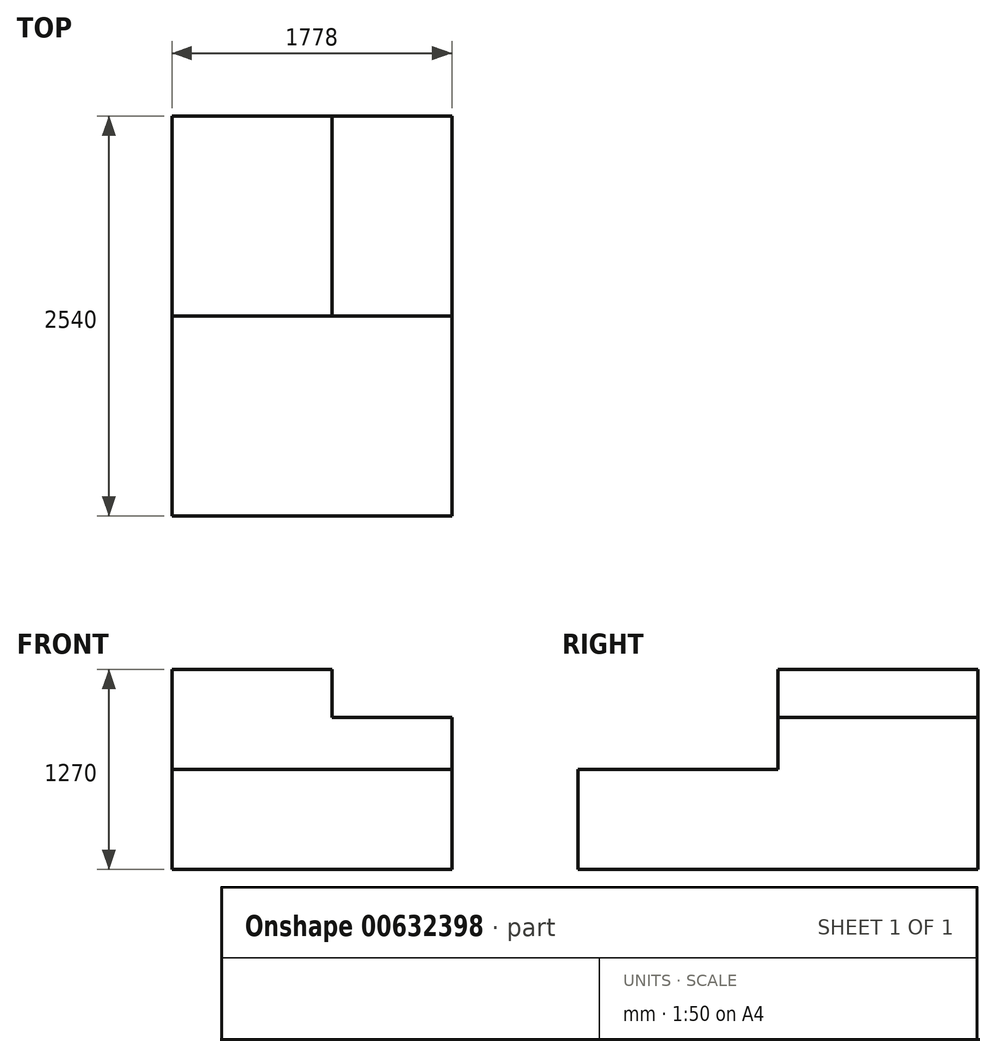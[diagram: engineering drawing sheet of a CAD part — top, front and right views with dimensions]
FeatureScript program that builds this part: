
annotation { "Feature Type Name" : "Feature", "Feature Type Description" : "" }
export const myFeature = defineFeature(function(context is Context, id is Id, definition is map)
    precondition{}
    {
        {
            var Q0;
            Q0=qCreatedBy(makeId("Right.planeOp"),FACE);
            var sketch = newSketch(context, id + "F0", { "sketchPlane" : qUnion([Q0])});
            skLineSegment(sketch, "E0", {"start": v(-399.09, -209.08) * mm, "end": v(2140.91, -209.08) * mm});
            skLineSegment(sketch, "E1", {"start": v(2140.91, -209.08) * mm, "end": v(2140.91, 756.12) * mm});
            skLineSegment(sketch, "E2", {"start": v(2140.91, 756.12) * mm, "end": v(870.91, 756.12) * mm});
            skLineSegment(sketch, "E3", {"start": v(870.91, 756.12) * mm, "end": v(870.91, 425.92) * mm});
            skLineSegment(sketch, "E4", {"start": v(870.91, 425.92) * mm, "end": v(-399.09, 425.92) * mm});
            skLineSegment(sketch, "E5", {"start": v(-399.09, 425.92) * mm, "end": v(-399.09, -209.08) * mm});
            skSolve(sketch);
        }
        {
            var Q0;
            Q0 = qSketchRegion(id + "F0", true);
            extrude(context, id + "F1", {"entities" : qUnion([Q0]), "depth" : 1778 * mm, "offsetDistance" : 25.4 * mm});
        }
        {
            var Q0;
            Q0=makeQuery(id+"F0.imprint","IMPRINT",FACE,{"disambiguationData":[TD([[makeQuery(id+"F0.imprint","IMPRINT",EDGE,{"derivedFrom":sQuery(id+"F0.wireOp",EDGE,"E0")}),1.0]])]});
            var sketch = newSketch(context, id + "F2", { "sketchPlane" : qUnion([Q0])});
            skLineSegment(sketch, "E6.0", {"start": v(2140.91, 756.12) * mm, "end": v(870.91, 756.12) * mm});
            skLineSegment(sketch, "E7", {"start": v(870.91, 756.12) * mm, "end": v(870.91, 1060.92) * mm});
            skLineSegment(sketch, "E8", {"start": v(870.91, 1060.92) * mm, "end": v(2140.91, 1060.92) * mm});
            skLineSegment(sketch, "E9", {"start": v(2140.91, 1060.92) * mm, "end": v(2140.91, 756.12) * mm});
            skSolve(sketch);
        }
        {
            var Q0;
            Q0 = qSketchRegion(id + "F2", true);
            extrude(context, id + "F3", {"entities" : qUnion([Q0]), "operationType" : NewBodyOperationType.ADD, "depth" : 1016 * mm, "offsetDistance" : 25.4 * mm});
        }
    });
